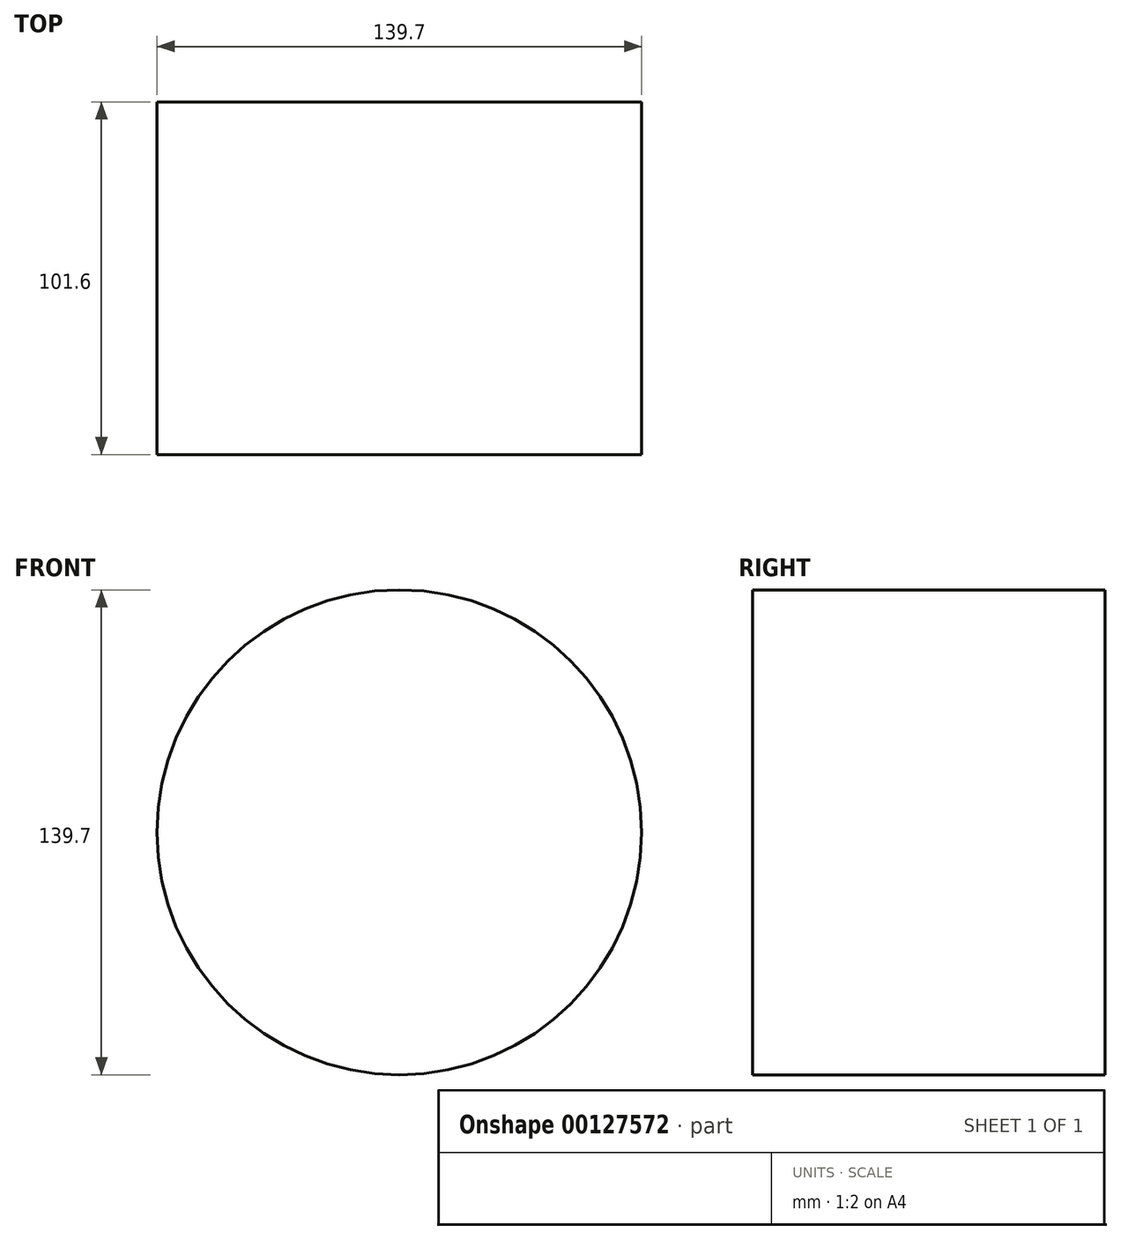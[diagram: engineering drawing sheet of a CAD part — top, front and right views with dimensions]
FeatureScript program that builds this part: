
annotation { "Feature Type Name" : "Feature", "Feature Type Description" : "" }
export const myFeature = defineFeature(function(context is Context, id is Id, definition is map)
    precondition{}
    {
        {
            var Q0;
            Q0=qCreatedBy(makeId("Front.planeOp"),FACE);
            var sketch = newSketch(context, id + "F0", { "sketchPlane" : qUnion([Q0])});
            skCircle(sketch, "E0", {"center": v(0, 0) * mm, "radius": 69.85 * mm});
            skSolve(sketch);
        }
        {
            var Q0;
            Q0=qSketchRegion(id+"F0",true);
            extrude(context, id + "F1", {"entities" : qUnion([Q0]), "depth" : 101.6 * mm});
        }
    });
